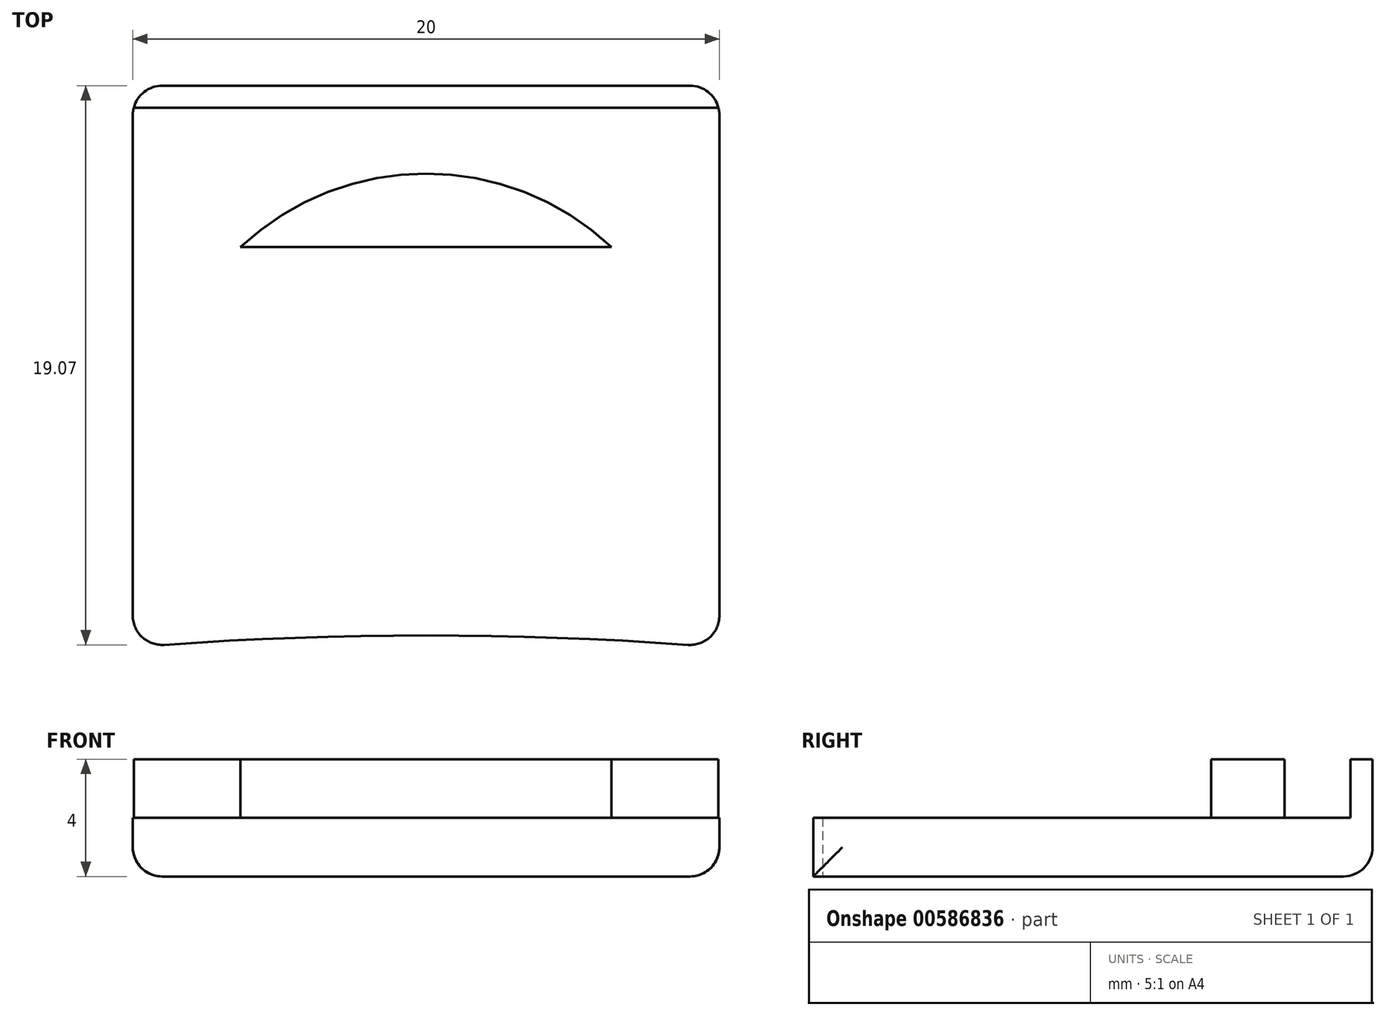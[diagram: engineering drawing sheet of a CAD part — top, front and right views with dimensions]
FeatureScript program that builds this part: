
annotation { "Feature Type Name" : "Feature", "Feature Type Description" : "" }
export const myFeature = defineFeature(function(context is Context, id is Id, definition is map)
    precondition{}
    {
        {
            var Q0;
            Q0=qCreatedBy(makeId("Top.planeOp"),FACE);
            var sketch = newSketch(context, id + "F0", { "sketchPlane" : qUnion([Q0])});
            skLineSegment(sketch, "E0.bottom", {"start": v(-10, 11) * mm, "end": v(10, 11) * mm});
            skLineSegment(sketch, "E0.top", {"start": v(-10, -11) * mm, "end": v(10, -11) * mm});
            skLineSegment(sketch, "E0.left", {"start": v(-10, 11) * mm, "end": v(-10, -11) * mm});
            skLineSegment(sketch, "E0.right", {"start": v(10, 11) * mm, "end": v(10, -11) * mm});
            skPoint(sketch, "E0.middle", {"position": v(0, 0) * mm});
            skSolve(sketch);
        }
        {
            var Q0;
            Q0 = qSketchRegion(id + "F0", true);
            extrude(context, id + "F1", {"entities" : qUnion([Q0]), "depth" : 2 * mm, "offsetDistance" : 25 * mm});
        }
        {
            var Q0;
            Q0=makeQuery(id+"F1.opExtrude","CAP_FACE",FACE,{"disambiguationData":[OSD([sQuery(id+"F0.wireOp",EDGE,"E0.bottom"),sQuery(id+"F0.wireOp",EDGE,"E0.top"),sQuery(id+"F0.wireOp",EDGE,"E0.left"),sQuery(id+"F0.wireOp",EDGE,"E0.right")])],"isStart":false});
            var sketch = newSketch(context, id + "F2", { "sketchPlane" : qUnion([Q0])});
            skCircle(sketch, "E1", {"center": v(0, -1.25) * mm, "radius": 9.25 * mm});
            skPoint(sketch, "E1.centerSnap0", {"position": v(0, -11) * mm});
            skSolve(sketch);
        }
        {
            var Q0;
            Q0=makeQuery(id+"F2.imprint","IMPRINT",FACE,{"disambiguationData":[TD([[makeQuery(id+"F2.imprint","IMPRINT",EDGE,{"derivedFrom":makeQuery(id+"F1.opExtrude","CAP_EDGE",EDGE,{"disambiguationData":[OSD([sQuery(id+"F0.wireOp",EDGE,"E0.bottom")])],"isStart":false})}),-1.0]])]});
            var sketch = newSketch(context, id + "F3", { "sketchPlane" : qUnion([Q0])});
            skLineSegment(sketch, "E2.bottom", {"start": v(10, -12.5) * mm, "end": v(-10, -12.5) * mm});
            skLineSegment(sketch, "E2.top", {"start": v(10, 5.5) * mm, "end": v(-10, 5.5) * mm});
            skLineSegment(sketch, "E2.left", {"start": v(10, -12.5) * mm, "end": v(10, 5.5) * mm});
            skLineSegment(sketch, "E2.right", {"start": v(-10, -12.5) * mm, "end": v(-10, 5.5) * mm});
            skPoint(sketch, "E2.middle", {"position": v(0, -3.5) * mm});
            skSolve(sketch);
        }
        {
            var Q0;
            Q0 = qSketchRegion(id + "F2", true);
            extrude(context, id + "F4", {"entities" : qUnion([Q0]), "operationType" : NewBodyOperationType.ADD, "depth" : 2 * mm, "offsetDistance" : 25 * mm});
        }
        {
            var Q0;
            Q0 = qSketchRegion(id + "F3", true);
            extrude(context, id + "F5", {"entities" : qUnion([Q0]), "operationType" : NewBodyOperationType.REMOVE, "depth" : 2 * mm, "offsetDistance" : 25 * mm});
        }
        {
            var Q0;
            Q0=makeQuery(id+"F5.boolean.opBoolean","MERGE",FACE,{"derivedFrom":[makeQuery(id+"F1.opExtrude","CAP_FACE",FACE,{"disambiguationData":[OSD([sQuery(id+"F0.wireOp",EDGE,"E0.bottom"),sQuery(id+"F0.wireOp",EDGE,"E0.top"),sQuery(id+"F0.wireOp",EDGE,"E0.left"),sQuery(id+"F0.wireOp",EDGE,"E0.right")])],"isStart":false}),makeQuery(id+"F5.opExtrude","CAP_FACE",FACE,{"disambiguationData":[OSD([sQuery(id+"F3.wireOp",EDGE,"E2.bottom"),sQuery(id+"F3.wireOp",EDGE,"E2.top"),sQuery(id+"F3.wireOp",EDGE,"E2.left"),sQuery(id+"F3.wireOp",EDGE,"E2.right")])],"isStart":true})]});
            var sketch = newSketch(context, id + "F6", { "sketchPlane" : qUnion([Q0])});
            skLineSegment(sketch, "E3.bottom", {"start": v(-10, 11) * mm, "end": v(10, 11) * mm});
            skLineSegment(sketch, "E3.top", {"start": v(-10, 10.25) * mm, "end": v(10, 10.25) * mm});
            skLineSegment(sketch, "E3.left", {"start": v(-10, 11) * mm, "end": v(-10, 10.25) * mm});
            skLineSegment(sketch, "E3.right", {"start": v(10, 11) * mm, "end": v(10, 10.25) * mm});
            skSolve(sketch);
        }
        {
            var Q0;
            Q0 = qSketchRegion(id + "F6", true);
            extrude(context, id + "F7", {"entities" : qUnion([Q0]), "operationType" : NewBodyOperationType.ADD, "depth" : 2 * mm, "offsetDistance" : 25 * mm});
        }
        {
            var Q0;
            Q0=qCreatedBy(makeId("Top.planeOp"),FACE);
            var sketch = newSketch(context, id + "F8", { "sketchPlane" : qUnion([Q0])});
            skCircle(sketch, "E4", {"center": v(0, -132.75) * mm, "radius": 125 * mm});
            skSolve(sketch);
        }
        {
            var Q0;
            Q0 = qSketchRegion(id + "F8", true);
            extrude(context, id + "F9", {"entities" : qUnion([Q0]), "operationType" : NewBodyOperationType.REMOVE, "depth" : 2 * mm, "offsetDistance" : 25 * mm});
        }
        {
            var Q0;
            Q0=makeQuery(id+"F9.boolean.opBoolean","INTERSECT",EDGE,{"derivedFrom":[makeQuery(id+"F7.boolean.opBoolean","MERGE",FACE,{"derivedFrom":[makeQuery(id+"F1.opExtrude","SWEPT_FACE",FACE,{"disambiguationData":[OSD([sQuery(id+"F0.wireOp",EDGE,"E0.right")])]}),makeQuery(id+"F7.opExtrude","SWEPT_FACE",FACE,{"disambiguationData":[OSD([sQuery(id+"F6.wireOp",EDGE,"E3.right")])]})]}),makeQuery(id+"F9.opExtrude","SWEPT_FACE",FACE,{"disambiguationData":[OSD([sQuery(id+"F8.wireOp",EDGE,"E4")])]})]});
            var Q1;
            Q1=makeQuery(id+"F9.boolean.opBoolean","INTERSECT",EDGE,{"derivedFrom":[makeQuery(id+"F7.boolean.opBoolean","MERGE",FACE,{"derivedFrom":[makeQuery(id+"F1.opExtrude","SWEPT_FACE",FACE,{"disambiguationData":[OSD([sQuery(id+"F0.wireOp",EDGE,"E0.left")])]}),makeQuery(id+"F7.opExtrude","SWEPT_FACE",FACE,{"disambiguationData":[OSD([sQuery(id+"F6.wireOp",EDGE,"E3.left")])]})]}),makeQuery(id+"F9.opExtrude","SWEPT_FACE",FACE,{"disambiguationData":[OSD([sQuery(id+"F8.wireOp",EDGE,"E4")])]})]});
            var Q2;
            Q2=makeQuery(id+"F7.boolean.opBoolean","MERGE",EDGE,{"derivedFrom":[makeQuery(id+"F1.opExtrude","SWEPT_EDGE",EDGE,{"disambiguationData":[OSD([sQuery(id+"F0.wireOp",EDGE,"E0.bottom"),sQuery(id+"F0.wireOp",EDGE,"E0.right")])]}),makeQuery(id+"F7.opExtrude","SWEPT_EDGE",EDGE,{"disambiguationData":[OSD([sQuery(id+"F6.wireOp",EDGE,"E3.bottom"),sQuery(id+"F6.wireOp",EDGE,"E3.right")])]})]});
            var Q3;
            Q3=makeQuery(id+"F7.boolean.opBoolean","MERGE",EDGE,{"derivedFrom":[makeQuery(id+"F1.opExtrude","SWEPT_EDGE",EDGE,{"disambiguationData":[OSD([sQuery(id+"F0.wireOp",EDGE,"E0.bottom"),sQuery(id+"F0.wireOp",EDGE,"E0.left")])]}),makeQuery(id+"F7.opExtrude","SWEPT_EDGE",EDGE,{"disambiguationData":[OSD([sQuery(id+"F6.wireOp",EDGE,"E3.bottom"),sQuery(id+"F6.wireOp",EDGE,"E3.left")])]})]});
            var Q4;
            Q4=makeQuery(id+"F1.opExtrude","CAP_EDGE",EDGE,{"disambiguationData":[OSD([sQuery(id+"F0.wireOp",EDGE,"E0.bottom")])],"isStart":true});
            var Q5;
            Q5=makeQuery(id+"F1.opExtrude","CAP_EDGE",EDGE,{"disambiguationData":[OSD([sQuery(id+"F0.wireOp",EDGE,"E0.left")])],"isStart":true});
            var Q6;
            Q6=makeQuery(id+"F9.boolean.opBoolean","COPY",EDGE,{"derivedFrom":makeQuery(id+"F9.opExtrude","CAP_EDGE",EDGE,{"disambiguationData":[OSD([sQuery(id+"F8.wireOp",EDGE,"E4")])],"isStart":true})});
            var Q7;
            Q7=makeQuery(id+"F1.opExtrude","CAP_EDGE",EDGE,{"disambiguationData":[OSD([sQuery(id+"F0.wireOp",EDGE,"E0.right")])],"isStart":true});
            fillet(context, id + "F10", {"entities" : qUnion([Q0, Q1, Q2, Q3, Q4, Q5, Q6, Q7]), "radius" : 1 * mm, "tangentPropagation" : true, "allowEdgeOverflow" : false});
        }
    });
